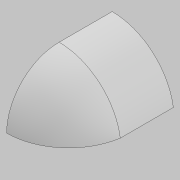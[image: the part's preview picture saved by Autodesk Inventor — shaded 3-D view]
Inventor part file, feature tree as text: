
AUTODESK INVENTOR PART (.ipt)
format: ipt  version: 2021 (Build 250183000, 183)  size: 129,536 bytes
history: native  units: mm
features: sketch x3, other x2, extrude x2, revolve x1
ambient origin geometry x8: Origin, YZ Plane, XZ Plane, XY Plane, X Axis, Y Axis, Z Axis, Center Point
bodies: Body1 (feature_tree)
feature tree (8):
  revolve  "Revolution2"  [1 undecoded]
  other  "end1"
  extrude  "Extrusion1"  Depth=160.0mm
  other  "end2"
  extrude  "Extrusion2"  Depth=10.0mm
  sketch  "Sketch1"  dims[d0=0.0mm d1=0.0mm]
  sketch  "Sketch3"  dims[d2=0.0mm d3=160.0mm]
  sketch  "Sketch4"  dims[d6=890.0mm d8=1037.737925mm d10=0.0mm d11=10.0mm d12=0.0mm d13=90.0deg d14=1037.737925mm d15=0.0mm d16=900.0mm d17=0.0mm d9=0.872665mm]
note: 1 required parameter value undecoded (feature->parameter linkage not recoverable at this tier; creation-order binding heuristic only, values carry confidence <= 0.55)
